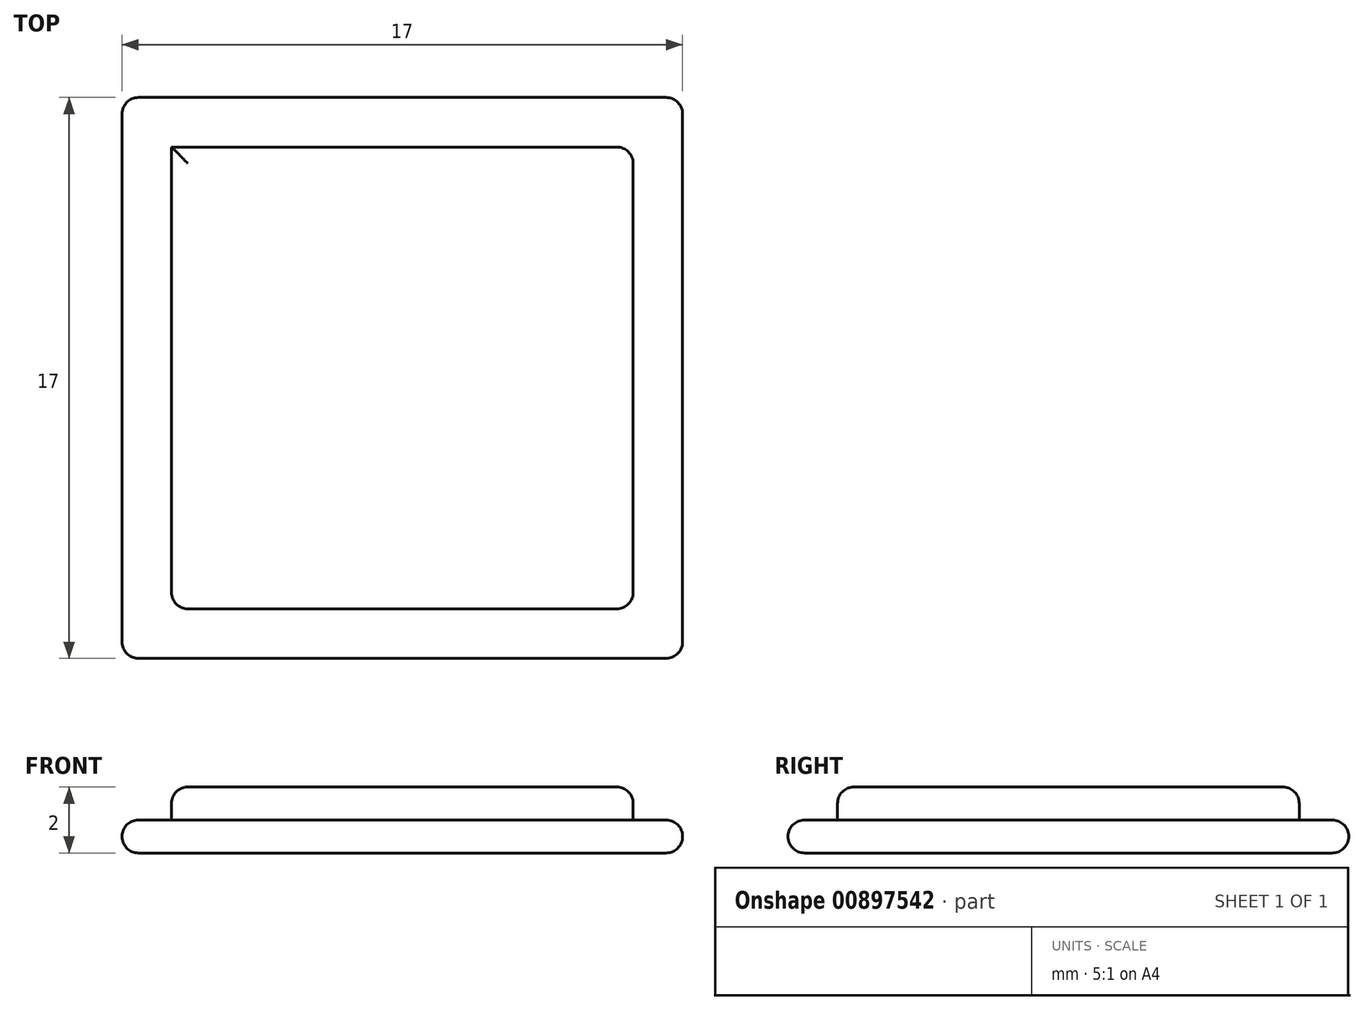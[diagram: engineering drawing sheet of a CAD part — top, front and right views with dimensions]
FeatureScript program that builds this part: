
annotation { "Feature Type Name" : "Feature", "Feature Type Description" : "" }
export const myFeature = defineFeature(function(context is Context, id is Id, definition is map)
    precondition{}
    {
        {
            var Q0;
            Q0=qCreatedBy(makeId("Top.planeOp"),FACE);
            var sketch = newSketch(context, id + "F0", { "sketchPlane" : qUnion([Q0])});
            skLineSegment(sketch, "E0.bottom", {"start": v(-45.96, 27.16) * mm, "end": v(-28.96, 27.16) * mm});
            skLineSegment(sketch, "E0.top", {"start": v(-45.96, 10.16) * mm, "end": v(-28.96, 10.16) * mm});
            skLineSegment(sketch, "E0.left", {"start": v(-45.96, 27.16) * mm, "end": v(-45.96, 10.16) * mm});
            skLineSegment(sketch, "E0.right", {"start": v(-28.96, 27.16) * mm, "end": v(-28.96, 10.16) * mm});
            skSolve(sketch);
        }
        {
            var Q0;
            Q0 = qSketchRegion(id + "F0", true);
            extrude(context, id + "F1", {"entities" : qUnion([Q0]), "depth" : 1 * mm, "offsetDistance" : 25 * mm});
        }
        {
            var Q0;
            Q0=makeQuery(id+"F1.opExtrude","CAP_FACE",FACE,{"disambiguationData":[OSD([sQuery(id+"F0.wireOp",EDGE,"E0.bottom"),sQuery(id+"F0.wireOp",EDGE,"E0.top"),sQuery(id+"F0.wireOp",EDGE,"E0.left"),sQuery(id+"F0.wireOp",EDGE,"E0.right")])],"isStart":false});
            var sketch = newSketch(context, id + "F2", { "sketchPlane" : qUnion([Q0])});
            skLineSegment(sketch, "E1.bottom", {"start": v(-45.96, 27.16) * mm, "end": v(-28.96, 27.16) * mm});
            skLineSegment(sketch, "E1.top", {"start": v(-45.96, 10.16) * mm, "end": v(-28.96, 10.16) * mm});
            skLineSegment(sketch, "E1.left", {"start": v(-45.96, 27.16) * mm, "end": v(-45.96, 10.16) * mm});
            skLineSegment(sketch, "E1.right", {"start": v(-28.96, 27.16) * mm, "end": v(-28.96, 10.16) * mm});
            skLineSegment(sketch, "E2.0", {"start": v(-44.46, 25.66) * mm, "end": v(-44.46, 11.66) * mm});
            skLineSegment(sketch, "E2.1", {"start": v(-30.46, 25.66) * mm, "end": v(-44.46, 25.66) * mm});
            skLineSegment(sketch, "E2.2", {"start": v(-30.46, 11.66) * mm, "end": v(-30.46, 25.66) * mm});
            skLineSegment(sketch, "E2.3", {"start": v(-44.46, 11.66) * mm, "end": v(-30.46, 11.66) * mm});
            skSolve(sketch);
        }
        {
            var Q0;
            Q0=makeQuery(id+"F2.imprint","IMPRINT",FACE,{"disambiguationData":[TD([[makeQuery(id+"F2.imprint","IMPRINT",EDGE,{"derivedFrom":sQuery(id+"F2.wireOp",EDGE,"E2.0")}),1.0]])]});
            extrude(context, id + "F3", {"entities" : qUnion([Q0]), "operationType" : NewBodyOperationType.ADD, "depth" : 1 * mm, "offsetDistance" : 25 * mm});
        }
        {
            var Q0;
            Q0=makeQuery(id+"F3.opExtrude","CAP_EDGE",EDGE,{"disambiguationData":[OSD([sQuery(id+"F2.wireOp",EDGE,"E2.1")])],"isStart":false});
            var Q1;
            Q1=makeQuery(id+"F3.opExtrude","CAP_EDGE",EDGE,{"disambiguationData":[OSD([sQuery(id+"F2.wireOp",EDGE,"E2.0")])],"isStart":false});
            var Q2;
            Q2=makeQuery(id+"F3.opExtrude","CAP_EDGE",EDGE,{"disambiguationData":[OSD([sQuery(id+"F2.wireOp",EDGE,"E2.0")])],"isStart":true});
            var Q3;
            Q3=makeQuery(id+"F3.opExtrude","CAP_EDGE",EDGE,{"disambiguationData":[OSD([sQuery(id+"F2.wireOp",EDGE,"E2.1")])],"isStart":true});
            var Q4;
            Q4=makeQuery(id+"F3.opExtrude","CAP_EDGE",EDGE,{"disambiguationData":[OSD([sQuery(id+"F2.wireOp",EDGE,"E2.3")])],"isStart":false});
            var Q5;
            Q5=makeQuery(id+"F1.opExtrude","CAP_EDGE",EDGE,{"disambiguationData":[OSD([sQuery(id+"F0.wireOp",EDGE,"E0.top")])],"isStart":false});
            var Q6;
            Q6=makeQuery(id+"F1.opExtrude","CAP_EDGE",EDGE,{"disambiguationData":[OSD([sQuery(id+"F0.wireOp",EDGE,"E0.left")])],"isStart":false});
            var Q7;
            Q7=makeQuery(id+"F1.opExtrude","CAP_EDGE",EDGE,{"disambiguationData":[OSD([sQuery(id+"F0.wireOp",EDGE,"E0.left")])],"isStart":true});
            var Q8;
            Q8=makeQuery(id+"F1.opExtrude","SWEPT_EDGE",EDGE,{"disambiguationData":[OSD([sQuery(id+"F0.wireOp",EDGE,"E0.bottom"),sQuery(id+"F0.wireOp",EDGE,"E0.left")])]});
            var Q9;
            Q9=makeQuery(id+"F1.opExtrude","CAP_EDGE",EDGE,{"disambiguationData":[OSD([sQuery(id+"F0.wireOp",EDGE,"E0.bottom")])],"isStart":false});
            var Q10;
            Q10=makeQuery(id+"F1.opExtrude","CAP_EDGE",EDGE,{"disambiguationData":[OSD([sQuery(id+"F0.wireOp",EDGE,"E0.bottom")])],"isStart":true});
            var Q11;
            Q11=makeQuery(id+"F3.opExtrude","CAP_EDGE",EDGE,{"disambiguationData":[OSD([sQuery(id+"F2.wireOp",EDGE,"E2.2")])],"isStart":true});
            var Q12;
            Q12=makeQuery(id+"F3.opExtrude","CAP_EDGE",EDGE,{"disambiguationData":[OSD([sQuery(id+"F2.wireOp",EDGE,"E2.2")])],"isStart":false});
            var Q13;
            Q13=makeQuery(id+"F3.opExtrude","SWEPT_EDGE",EDGE,{"disambiguationData":[OSD([sQuery(id+"F2.wireOp",EDGE,"E2.1"),sQuery(id+"F2.wireOp",EDGE,"E2.2")])]});
            var Q14;
            Q14=makeQuery(id+"F1.opExtrude","CAP_EDGE",EDGE,{"disambiguationData":[OSD([sQuery(id+"F0.wireOp",EDGE,"E0.right")])],"isStart":false});
            var Q15;
            Q15=makeQuery(id+"F1.opExtrude","CAP_EDGE",EDGE,{"disambiguationData":[OSD([sQuery(id+"F0.wireOp",EDGE,"E0.right")])],"isStart":true});
            var Q16;
            Q16=makeQuery(id+"F1.opExtrude","SWEPT_EDGE",EDGE,{"disambiguationData":[OSD([sQuery(id+"F0.wireOp",EDGE,"E0.bottom"),sQuery(id+"F0.wireOp",EDGE,"E0.right")])]});
            var Q17;
            Q17=makeQuery(id+"F1.opExtrude","SWEPT_EDGE",EDGE,{"disambiguationData":[OSD([sQuery(id+"F0.wireOp",EDGE,"E0.top"),sQuery(id+"F0.wireOp",EDGE,"E0.right")])]});
            var Q18;
            Q18=makeQuery(id+"F1.opExtrude","SWEPT_EDGE",EDGE,{"disambiguationData":[OSD([sQuery(id+"F0.wireOp",EDGE,"E0.top"),sQuery(id+"F0.wireOp",EDGE,"E0.left")])]});
            var Q19;
            Q19=makeQuery(id+"F1.opExtrude","CAP_EDGE",EDGE,{"disambiguationData":[OSD([sQuery(id+"F0.wireOp",EDGE,"E0.top")])],"isStart":true});
            var Q20;
            Q20=makeQuery(id+"F3.opExtrude","CAP_EDGE",EDGE,{"disambiguationData":[OSD([sQuery(id+"F2.wireOp",EDGE,"E2.3")])],"isStart":true});
            var Q21;
            Q21=makeQuery(id+"F3.opExtrude","SWEPT_EDGE",EDGE,{"disambiguationData":[OSD([sQuery(id+"F2.wireOp",EDGE,"E2.0"),sQuery(id+"F2.wireOp",EDGE,"E2.3")])]});
            var Q22;
            Q22=makeQuery(id+"F3.opExtrude","SWEPT_EDGE",EDGE,{"disambiguationData":[OSD([sQuery(id+"F2.wireOp",EDGE,"E2.2"),sQuery(id+"F2.wireOp",EDGE,"E2.3")])]});
            fillet(context, id + "F4", {"entities" : qUnion([Q0, Q1, Q2, Q3, Q4, Q5, Q6, Q7, Q8, Q9, Q10, Q11, Q12, Q13, Q14, Q15, Q16, Q17, Q18, Q19, Q20, Q21, Q22]), "radius" : 0.5 * mm, "tangentPropagation" : true, "allowEdgeOverflow" : false});
        }
    });
